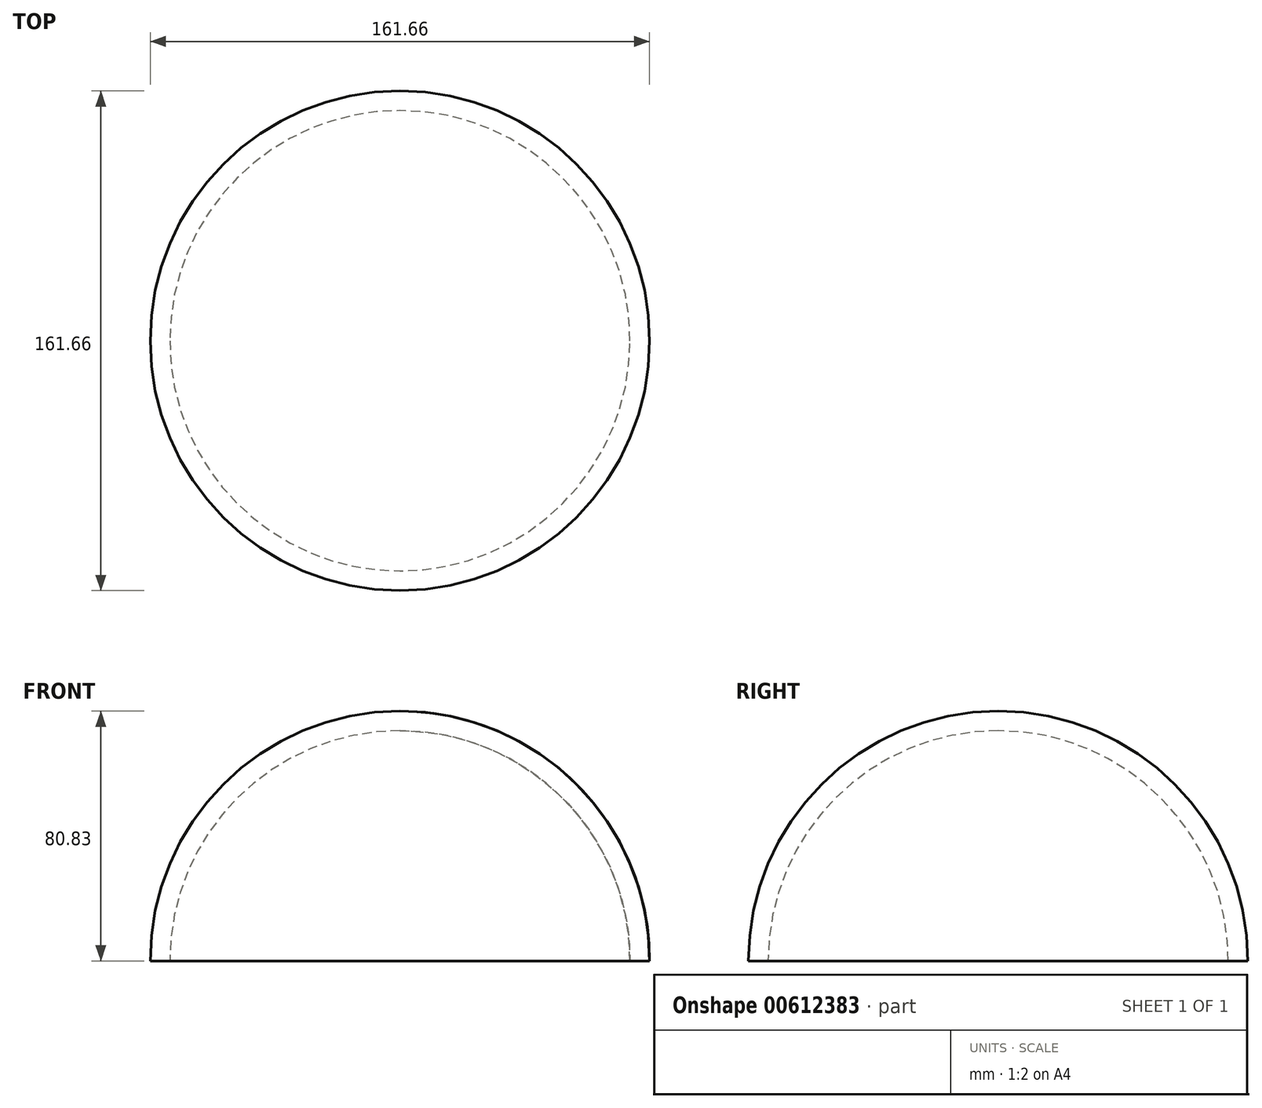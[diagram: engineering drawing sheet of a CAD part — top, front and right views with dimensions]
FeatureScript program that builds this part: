
annotation { "Feature Type Name" : "Feature", "Feature Type Description" : "" }
export const myFeature = defineFeature(function(context is Context, id is Id, definition is map)
    precondition{}
    {
        {
            var Q0;
            Q0=qCreatedBy(makeId("Front.planeOp"),FACE);
            var sketch = newSketch(context, id + "F0", { "sketchPlane" : qUnion([Q0])});
            skArc(sketch, "E0", {"start": v(74.48, 0) * mm, "mid": v(52.66, 52.66) * mm, "end": v(0, 74.48) * mm});
            skArc(sketch, "E1.0", {"start": v(80.83, 0) * mm, "mid": v(57.15, 57.15) * mm, "end": v(0, 80.83) * mm});
            skLineSegment(sketch, "E2", {"start": v(74.48, 0) * mm, "end": v(80.83, 0) * mm});
            skLineSegment(sketch, "E3", {"start": v(0, 80.83) * mm, "end": v(0, 74.48) * mm});
            skLineSegment(sketch, "E4", {"start": v(0, 0) * mm, "end": v(0, 74.48) * mm, "construction": true});
            skSolve(sketch);
        }
        {
            var Q0;
            Q0 = qSketchRegion(id + "F0", true);
            var Q1;
            Q1=sQuery(id+"F0.wireOp",EDGE,"E4");
            revolve(context, id + "F1", {"entities" : qUnion([Q0]), "axis" : qUnion([Q1]), "revolveType" : RevolveType.FULL});
        }
    });
